FCSTD DOCUMENT  (FreeCAD 0.19R24276 (Git))
Label: Master_sketch_revolution_rotation
License: All rights reserved
LicenseURL: http://en.wikipedia.org/wiki/All_rights_reserved
objects: Sketcher::SketchObject×1, PartDesign::Body×1
note: 2 computed .brp shape members not serialized (recipe doc carries the construction recipe); baked Part::Feature solids carry a one-line shape summary decoded from their .brp

FEATURE [Sketcher::SketchObject] Sketch
  FullyConstrained = false
  MapMode = 5
  Support = -> [XY_Plane]
  sketch-geometry (49):
    g0: Circle CenterX=-0.176014 CenterY=-53.9997 CenterZ=0 NormalX=0 NormalY=0 NormalZ=1 AngleXU=0 Radius=4
    g1: LineSegment StartX=-57.9202 StartY=-39.2908 StartZ=0 EndX=-1.42136 EndY=-57.8009 EndZ=0
    g2: LineSegment StartX=-44.9998 StartY=0.146678 StartZ=0 EndX=-57.9202 EndY=-39.2908 EndZ=0
    g3: LineSegment StartX=-0.176014 StartY=-53.9997 StartZ=0 EndX=-1.42136 EndY=-57.8009 EndZ=0
    g4: LineSegment StartX=1.04453 StartY=-57.8089 StartZ=0 EndX=57.6629 EndY=-39.6675 EndZ=0
    g5: LineSegment StartX=44.9998 StartY=-0.146678 StartZ=0 EndX=57.6629 EndY=-39.6675 EndZ=0
    g6: LineSegment StartX=-0.176014 StartY=-53.9997 StartZ=0 EndX=1.04453 EndY=-57.8089 EndZ=0
    g7: LineSegment StartX=-44.9998 StartY=0.146678 StartZ=0 EndX=44.9998 EndY=-0.146678 EndZ=0
    g8: LineSegment StartX=0 StartY=0 StartZ=0 EndX=-0.176014 EndY=-53.9997 EndZ=0
    g9: Circle CenterX=0 CenterY=0 CenterZ=0 NormalX=0 NormalY=0 NormalZ=1 AngleXU=0 Radius=90
    g10: LineSegment StartX=-44.9998 StartY=0.146678 StartZ=0 EndX=-31.8819 EndY=-39.2255 EndZ=0
    g11: Circle CenterX=0.176014 CenterY=53.9997 CenterZ=0 NormalX=0 NormalY=0 NormalZ=1 AngleXU=0 Radius=4
    g12: LineSegment StartX=0 StartY=0 StartZ=0 EndX=0.176014 EndY=53.9997 EndZ=0
    g13: Circle CenterX=0 CenterY=220 CenterZ=0 NormalX=0 NormalY=0 NormalZ=1 AngleXU=0 Radius=20
    g14: LineSegment StartX=-44.9998 StartY=0.146678 StartZ=0 EndX=-54.9029 EndY=-40.1544 EndZ=0
    g15: LineSegment StartX=44.9998 StartY=-0.146678 StartZ=0 EndX=54.9029 EndY=40.1544 EndZ=0
    g16: LineSegment StartX=312.32 StartY=347.802 StartZ=0 EndX=312.32 EndY=297.802 EndZ=0
    g17: LineSegment StartX=0 StartY=0 StartZ=0 EndX=558.32 EndY=0 EndZ=0
    g18: LineSegment StartX=558.32 StartY=0 StartZ=0 EndX=558.32 EndY=303.26 EndZ=0
    g19: LineSegment StartX=312.32 StartY=347.802 StartZ=0 EndX=656.72 EndY=285.443 EndZ=0
    g20: LineSegment StartX=632.368 StartY=72.3118 StartZ=0 EndX=558.32 EndY=0 EndZ=0
    g21: LineSegment StartX=558.32 StartY=303.26 StartZ=0 EndX=558.32 EndY=253.26 EndZ=0
    g22: LineSegment StartX=312.32 StartY=297.802 StartZ=0 EndX=558.32 EndY=253.26 EndZ=0
    g23: LineSegment StartX=-29.9303 StartY=-48.4608 StartZ=0 EndX=-27.1283 EndY=-39.9081 EndZ=0
    g24: LineSegment StartX=-29.9303 StartY=-48.4608 StartZ=0 EndX=-32.7324 EndY=-57.0135 EndZ=0
    g25: Circle CenterX=-75.5057 CenterY=-210.688 CenterZ=0 NormalX=0 NormalY=0 NormalZ=1 AngleXU=0 Radius=10
    g26: Circle CenterX=80 CenterY=-210.485 CenterZ=0 NormalX=0 NormalY=0 NormalZ=1 AngleXU=0 Radius=10
    g27: Circle CenterX=-80 CenterY=-260.485 CenterZ=0 NormalX=0 NormalY=0 NormalZ=1 AngleXU=0 Radius=10
    g28: LineSegment StartX=80 StartY=-210.485 StartZ=0 EndX=80 EndY=-260.485 EndZ=0
    g29: LineSegment StartX=-80 StartY=-260.485 StartZ=0 EndX=-75.5057 EndY=-210.688 EndZ=0
    g30: Circle CenterX=80 CenterY=-260.485 CenterZ=0 NormalX=0 NormalY=0 NormalZ=1 AngleXU=0 Radius=50.9884
    g31: Circle CenterX=-44.9998 CenterY=0.146678 CenterZ=0 NormalX=0 NormalY=0 NormalZ=1 AngleXU=0 Radius=41.5
    g32: LineSegment StartX=80 StartY=-260.485 StartZ=0 EndX=-80 EndY=-260.485 EndZ=0
    g33: Circle CenterX=44.9998 CenterY=-0.146678 CenterZ=0 NormalX=0 NormalY=0 NormalZ=1 AngleXU=0 Radius=41.5
    g34: LineSegment StartX=0 StartY=-162.685 StartZ=0 EndX=0 EndY=-260.485 EndZ=0
    g35: Circle CenterX=0 CenterY=-211.215 CenterZ=0 NormalX=0 NormalY=0 NormalZ=1 AngleXU=0 Radius=10
    g36: LineSegment StartX=0 StartY=-260.485 StartZ=0 EndX=0 EndY=-211.215 EndZ=0
    g37: Circle CenterX=-44.1986 CenterY=-222.275 CenterZ=0 NormalX=0 NormalY=0 NormalZ=1 AngleXU=0 Radius=10
    g38: LineSegment StartX=-44.1986 StartY=-222.275 StartZ=0 EndX=-44.1986 EndY=-260.485 EndZ=0
    g39: LineSegment StartX=-67.8639 StartY=-204.238 StartZ=0 EndX=-44.1986 EndY=-232.275 EndZ=0
    g40: LineSegment StartX=-44.1986 StartY=-232.275 StartZ=0 EndX=-44.1986 EndY=-232.275 EndZ=0
    g41: LineSegment StartX=-44.1986 StartY=-232.275 StartZ=0 EndX=-6.0547 EndY=-203.257 EndZ=0
    g42: LineSegment StartX=-6.0547 StartY=-203.257 StartZ=0 EndX=1.13095 EndY=-201.279 EndZ=0
    g43: LineSegment StartX=1.13095 StartY=-201.279 StartZ=0 EndX=79.8992 EndY=-200.486 EndZ=0
    g44: LineSegment StartX=90 StartY=-210.485 StartZ=0 EndX=79.8992 EndY=-200.486 EndZ=0
    g45: LineSegment StartX=90 StartY=-210.485 StartZ=0 EndX=90 EndY=-210.487 EndZ=0
    g46: LineSegment StartX=90 StartY=-210.487 StartZ=0 EndX=29.9221 EndY=-250.893 EndZ=0
    g47: LineSegment StartX=29.9221 StartY=-250.893 StartZ=0 EndX=-82.8248 EndY=-250.893 EndZ=0
    g48: LineSegment StartX=-44.1986 StartY=-222.275 StartZ=0 EndX=-44.1986 EndY=-232.275 EndZ=0
  constraints (111):
    c: Diameter(g0) = 8
    c: PointOnObject(g1,g0)
    c: Coincident(g2,g1)
    c: Perpendicular(g1,g2)
    c: Coincident(g3,g0)
    c: Coincident(g3,g1)
    c: Perpendicular(g3,g1)
    c: PointOnObject(g4,g0)
    c: Coincident(g5,g4)
    c: Perpendicular(g5,g4)
    c: Coincident(g6,g0)
    c: Coincident(g6,g4)
    c: Perpendicular(g4,g6)
    c: Distance(g7) = 90
    c: Coincident(g8,g-1)
    c: Coincident(g8,g0)
    c: Perpendicular(g7,g8)
    c: Distance(g8) = 54
    c: Coincident(g9,g-1)
    c: Diameter(g9) = 180
    c: Equal(g0,g11)
    c: Coincident(g12,g-1)
    c: Coincident(g12,g11)
    c: Equal(g12,g8)
    c: Parallel(g12,g8)
    c: PointOnObject(g13,g-2)
    c: Radius(g13) = 20
    c: DistanceY(g-1,g13) = 220
    c: Parallel(g14,g15)
    c: Vertical(g16)
    c: Coincident(g17,g-1)
    c: PointOnObject(g17,g-1)
    c: Coincident(g18,g17)
    c: Vertical(g18)
    c: Coincident(g19,g16)
    c: DistanceY(g16,g16) = 50
    c: DistanceX(g17,g17) = 558.32
    c: PointOnObject(g18,g19)
    c: DistanceY(g18,g18) = 303.26
    c: Distance(g18,g16) = 250
    c: Distance(g18,g19) = 100
    c: Coincident(g20,g17)
    c: Coincident(g21,g18)
    c: Coincident(g22,g16)
    c: Coincident(g22,g21)
    c: Equal(g16,g21)
    c: Vertical(g21)
    c: PointOnObject(g23,g1)
    c: Coincident(g24,g23)
    c: Symmetric(g24,g23,g23)
    c: Distance(g24,g23) = 18
    c: Perpendicular(g23,g1)
    c: Distance(g23,g1) = 30
    c: Diameter(g25) = 20
    c: Equal(g25,g26)
    c: Diameter(g27) = 20
    c: Coincident(g28,g26)
    c: Coincident(g29,g27)
    c: Equal(g28,g29)
    c: Distance(g29) = 50
    c: Coincident(g31,g2)
    c: Coincident(g32,g30)
    c: Coincident(g32,g27)
    c: Distance(g32) = 160
    c: Coincident(g28,g30)
    c: Coincident(g33,g5)
    c: Equal(g31,g33)
    c: Coincident(g29,g25)
    c: Horizontal(g32)
    c: PointOnObject(g34,g-2)
    c: Vertical(g34)
    c: Symmetric(g27,g28,g34)
    c: Angle(g28,g32) = 1.5708
    c: PointOnObject(g35,g-2)
    c: Coincident(g36,g34)
    c: Coincident(g36,g35)
    c: Coincident(g38,g37)
    c: PointOnObject(g38,g32)
    c: Vertical(g38)
    c: DistanceY(g38,g38) = 38.21
    c: DistanceY(g36,g36) = 49.27
    c: PointOnObject(g39,g25)
    c: PointOnObject(g39,g37)
    c: Tangent(g39,g25)
    c: Coincident(g40,g39)
    c: PointOnObject(g40,g37)
    c: Coincident(g41,g40)
    c: PointOnObject(g41,g35)
    c: Tangent(g41,g35)
    c: Coincident(g42,g41)
    c: PointOnObject(g42,g35)
    c: Coincident(g43,g42)
    c: PointOnObject(g43,g26)
    c: Tangent(g43,g26)
    c: PointOnObject(g44,g26)
    c: Coincident(g44,g43)
    c: Coincident(g45,g44)
    c: PointOnObject(g45,g30)
    c: Vertical(g45)
    c: Tangent(g45,g26)
    c: Coincident(g46,g45)
    c: PointOnObject(g46,g30)
    c: Coincident(g47,g46)
    c: PointOnObject(g47,g27)
    c: Horizontal(g47)
    c: Equal(g37,g25)
    c: Equal(g37,g35)
    c: Horizontal(g40)
    c: Coincident(g48,g37)
    c: Coincident(g48,g39)
    c: Vertical(g48)
FEATURE [PartDesign::Body] Body
  Group = -> [Sketch]
  Origin = -> Origin
